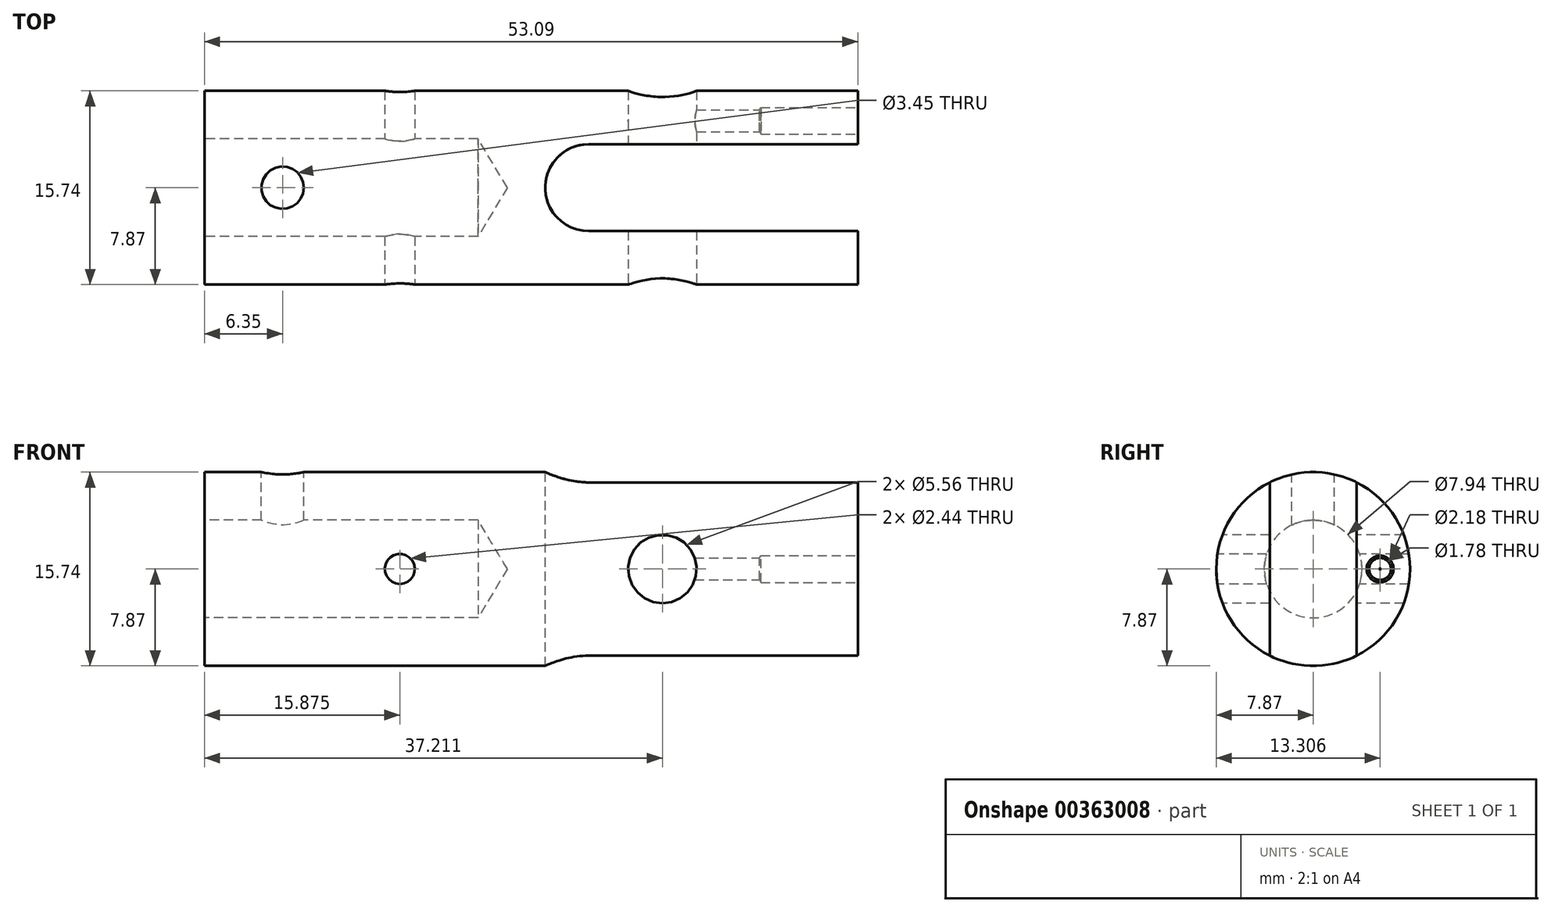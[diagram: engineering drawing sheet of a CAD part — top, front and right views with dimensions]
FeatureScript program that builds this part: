
annotation { "Feature Type Name" : "Feature", "Feature Type Description" : "" }
export const myFeature = defineFeature(function(context is Context, id is Id, definition is map)
    precondition{}
    {
        {
            var Q0;
            Q0=qCreatedBy(makeId("Right.planeOp"),FACE);
            var sketch = newSketch(context, id + "F0", { "sketchPlane" : qUnion([Q0])});
            skCircle(sketch, "E0", {"center": v(0, 0) * mm, "radius": 7.87 * mm});
            skSolve(sketch);
        }
        {
            var Q0;
            Q0=makeQuery(id+"F0.imprint","IMPRINT",FACE,{"disambiguationData":[TD([[makeQuery(id+"F0.imprint","IMPRINT",EDGE,{"derivedFrom":sQuery(id+"F0.wireOp",EDGE,"E0")}),1.0]])]});
            extrude(context, id + "F1", {"entities" : qUnion([Q0]), "depth" : 53.1 * mm});
        }
        {
            var Q0;
            Q0=qCreatedBy(makeId("Top.planeOp"),FACE);
            var sketch = newSketch(context, id + "F2", { "sketchPlane" : qUnion([Q0])});
            skLineSegment(sketch, "E1.0", {"start": v(31.22, -3.53) * mm, "end": v(67.76, -3.53) * mm});
            skLineSegment(sketch, "E2.0", {"start": v(31.22, 3.53) * mm, "end": v(67.76, 3.53) * mm});
            skLineSegment(sketch, "E3", {"start": v(67.76, 3.53) * mm, "end": v(67.76, -3.53) * mm});
            skArc(sketch, "E4", {"start": v(31.22, 3.53) * mm, "mid": v(27.69, 0) * mm, "end": v(31.22, -3.53) * mm});
            skSolve(sketch);
        }
        {
            var Q0;
            Q0=makeQuery(id+"F2.imprint","IMPRINT",FACE,{"disambiguationData":[TD([[makeQuery(id+"F2.imprint","IMPRINT",EDGE,{"derivedFrom":sQuery(id+"F2.wireOp",EDGE,"E1.0")}),1.0]])]});
            extrude(context, id + "F3", {"entities" : qUnion([Q0]), "operationType" : NewBodyOperationType.REMOVE, "endBound" : BoundingType.SYMMETRIC, "oppositeDirection" : true, "depth" : 25.4 * mm});
        }
        {
            var Q0;
            Q0=qCreatedBy(makeId("Top.planeOp"),FACE);
            cPlane(context, id + "F4", {"entities" : qUnion([Q0]), "cplaneType" : CPlaneType.OFFSET, "offset" : 11.94 * mm, "width" : 152.4 * mm, "height" : 152.4 * mm});
        }
        {
            var Q0;
            Q0=qCreatedBy(id+"F4.planeOp",FACE);
            var sketch = newSketch(context, id + "F5", { "sketchPlane" : qUnion([Q0])});
            skPoint(sketch, "E5", {"position": v(6.35, 0) * mm});
            skSolve(sketch);
        }
        {
            var Q0;
            Q0=sQuery(id+"F5.wireOp",VERTEX,"E5");
            var Q1;
            Q1=makeQuery(id+"F1.opExtrude","SWEPT_BODY",BODY,{"disambiguationData":[OSD([sQuery(id+"F0.wireOp",EDGE,"E0")])]});
            hole(context, id + "F6", {"style" : HoleStyle.SIMPLE, "endStyle" : HoleEndStyle.BLIND, "standardTappedOrClearance" : lookupTablePath({ "standard" : "ANSI", "engagement" : "75%", "pitch" : "32 tpi", "size" : "#8", "type" : "Tapped" }), "standardBlindInLast" : lookupTablePath({ "standard" : "ANSI", "engagement" : "75%", "pitch" : "32 tpi", "size" : "#8", "type" : "Tapped" }), "holeDiameter" : 3.45 * mm, "showTappedDepth" : true, "holeDepth" : 7.72 * mm, "tappedDepth" : 5.33 * mm, "tapClearance" : 3, "locations" : qUnion([Q0]), "scope" : qUnion([Q1]), "majorDiameter" : 4.17 * mm});
        }
        {
            var Q0;
            Q0=makeQuery(id+"F1.opExtrude","CAP_FACE",FACE,{"disambiguationData":[OSD([sQuery(id+"F0.wireOp",EDGE,"E0")])],"isStart":true});
            var sketch = newSketch(context, id + "F7", { "sketchPlane" : qUnion([Q0])});
            skPoint(sketch, "E6", {"position": v(0, 0) * mm});
            skSolve(sketch);
        }
        {
            var Q0;
            Q0=sQuery(id+"F7.wireOp",VERTEX,"E6");
            var Q1;
            Q1=makeQuery(id+"F1.opExtrude","SWEPT_BODY",BODY,{"disambiguationData":[OSD([sQuery(id+"F0.wireOp",EDGE,"E0")])]});
            hole(context, id + "F8", {"style" : HoleStyle.SIMPLE, "endStyle" : HoleEndStyle.BLIND, "holeDiameter" : 7.94 * mm, "holeDepth" : 22.22 * mm, "tappedDepth" : 5.34 * mm, "tapClearance" : 3, "locations" : qUnion([Q0]), "scope" : qUnion([Q1])});
        }
        {
            var Q0;
            Q0=qCreatedBy(makeId("Front.planeOp"),FACE);
            var sketch = newSketch(context, id + "F9", { "sketchPlane" : qUnion([Q0])});
            skCircle(sketch, "E7", {"center": v(37.21, 0) * mm, "radius": 2.78 * mm});
            skSolve(sketch);
        }
        {
            var Q0;
            Q0=makeQuery(id+"F9.imprint","IMPRINT",FACE,{"disambiguationData":[TD([[makeQuery(id+"F9.imprint","IMPRINT",EDGE,{"derivedFrom":sQuery(id+"F9.wireOp",EDGE,"E7")}),1.0]])]});
            extrude(context, id + "F10", {"entities" : qUnion([Q0]), "operationType" : NewBodyOperationType.REMOVE, "endBound" : BoundingType.SYMMETRIC, "oppositeDirection" : true, "depth" : 25.4 * mm});
        }
        {
            var Q0;
            Q0=qCreatedBy(makeId("Front.planeOp"),FACE);
            cPlane(context, id + "F11", {"entities" : qUnion([Q0]), "cplaneType" : CPlaneType.OFFSET, "offset" : 12.7 * mm, "width" : 152.4 * mm, "height" : 152.4 * mm});
        }
        {
            var Q0;
            Q0=qCreatedBy(id+"F11.planeOp",FACE);
            var sketch = newSketch(context, id + "F12", { "sketchPlane" : qUnion([Q0])});
            skPoint(sketch, "E8", {"position": v(15.88, 0) * mm});
            skSolve(sketch);
        }
        {
            var Q0;
            Q0=sQuery(id+"F12.wireOp",VERTEX,"E8");
            var Q1;
            Q1=makeQuery(id+"F1.opExtrude","SWEPT_BODY",BODY,{"disambiguationData":[OSD([sQuery(id+"F0.wireOp",EDGE,"E0")])]});
            hole(context, id + "F13", {"style" : HoleStyle.SIMPLE, "endStyle" : HoleEndStyle.THROUGH, "standardTappedOrClearance" : lookupTablePath({ "standard" : "ANSI", "size" : "#41 (0.1)", "type" : "Drilled" }), "standardBlindInLast" : lookupTablePath({ "standard" : "ANSI", "size" : "#41", "type" : "Drilled" }), "holeDiameter" : 2.44 * mm, "tappedDepth" : 5.33 * mm, "tapClearance" : 3, "locations" : qUnion([Q0]), "scope" : qUnion([Q1])});
        }
        {
            var Q0;
            {var subQ0=sQuery(id+"F0.wireOp",EDGE,"E0");Q0=makeQuery(id+"F3.boolean.opBoolean","SPLIT",FACE,{"disambiguationData":[TD([makeQuery(id+"F3.opExtrude","SWEPT_FACE",FACE,{"disambiguationData":[OSD([sQuery(id+"F2.wireOp",EDGE,"E2.0")])]})])],"derivedFrom":makeQuery(id+"F1.opExtrude","CAP_FACE",FACE,{"disambiguationData":[OSD([subQ0])],"isStart":false})});}
            var sketch = newSketch(context, id + "F14", { "sketchPlane" : qUnion([Q0])});
            skPoint(sketch, "E9", {"position": v(5.44, 0) * mm});
            skPoint(sketch, "E9.positionSnap0", {"position": v(3.53, 0) * mm});
            skSolve(sketch);
        }
        {
            var Q0;
            Q0=sQuery(id+"F14.wireOp",VERTEX,"E9");
            var Q1;
            Q1=makeQuery(id+"F1.opExtrude","SWEPT_BODY",BODY,{"disambiguationData":[OSD([sQuery(id+"F0.wireOp",EDGE,"E0")])]});
            hole(context, id + "F15", {"style" : HoleStyle.SIMPLE, "endStyle" : HoleEndStyle.BLIND, "standardTappedOrClearance" : lookupTablePath({ "standard" : "ANSI", "size" : "#44 (0.09)", "type" : "Drilled" }), "standardBlindInLast" : lookupTablePath({ "standard" : "ANSI", "size" : "#44", "type" : "Drilled" }), "holeDiameter" : 2.18 * mm, "holeDepth" : 7.87 * mm, "tappedDepth" : 5.33 * mm, "tapClearance" : 3, "locations" : qUnion([Q0]), "scope" : qUnion([Q1])});
        }
        {
            var Q0;
            Q0=sQuery(id+"F14.wireOp",VERTEX,"E9");
            var Q1;
            Q1=makeQuery(id+"F1.opExtrude","SWEPT_BODY",BODY,{"disambiguationData":[OSD([sQuery(id+"F0.wireOp",EDGE,"E0")])]});
            hole(context, id + "F16", {"style" : HoleStyle.SIMPLE, "endStyle" : HoleEndStyle.BLIND, "standardTappedOrClearance" : lookupTablePath({ "standard" : "ANSI", "engagement" : "75%", "pitch" : "56 tpi", "size" : "#2", "type" : "Tapped" }), "standardBlindInLast" : lookupTablePath({ "standard" : "ANSI", "engagement" : "75%", "pitch" : "56 tpi", "size" : "#2", "type" : "Tapped" }), "holeDiameter" : 1.78 * mm, "showTappedDepth" : true, "holeDepth" : 10.16 * mm, "tappedDepth" : 8.8 * mm, "tapClearance" : 3, "locations" : qUnion([Q0]), "scope" : qUnion([Q1]), "majorDiameter" : 2.18 * mm});
        }
    });
